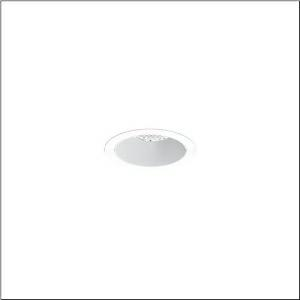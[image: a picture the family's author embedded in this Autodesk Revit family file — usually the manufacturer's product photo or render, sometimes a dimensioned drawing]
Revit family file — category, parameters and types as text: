
# Revit family: lunis_21_m_51db18ec91c
name_source: partatom
category: Lighting Fixtures
units: mm (PartAtom-declared; Revit-internal decimal feet)

## family parameters
Cut with Voids When Loaded = No
Host = Face
Light Source = No
Part Type = Normal
Room Calculation Point = No
Round Connector Dimension = Use Diameter
Shared = No

## types (1)
- --- (1 x LED, 3870 lm, 25.5 W, 6500K)
    Apparent Load = 26 VA
    CIE Flux Codes = 86 95 99 100 100
    Color Rendering = 80
    Color Temperature = 6500K
    Default Elevation = 1800 mm
    Description = Lunis 21 M, downlight, light control with lens, of PMMA, anti glare with reflector, of PC, light emission: direct distribution, LED rated luminous flux: 1.800lm, light colour: 830/840/865, with terminal, 5-pole, mains connection: 220..240V, AC/DC, 0/50..60Hz, housing, round, of diecast aluminium, traffic white (RAL 9016), diameter: 115mm, clamping range: 1..40mm, protection rating (complete): IP20, protection rating (on room side): IP54, insulation class (complete): insulation class II (safety insulation), certification: CE, impact resistance: IK03, packaging unit: 1 piece
    Height = 0 mm  [stored 0 ft]
    Lamp = 1 x LED
    Lamp Light Flux = 3870 lm
    Lamp Power = 25.5 W
    Lamp count = 1
    Length = 115 mm
    Luminous efficacy = 152 lm/W
    Manufacturer = Siteco
    ModVariant = No
    Model = 51DB18EC91C
    Mounting Place = Ceiling
    Mounting Type = Recessed
    Number of Poles = 1
    OnlyDefault = Yes
    Power Factor = 1
    Product Name = Lunis 21 M
    Product group = downlight
    ProductGroupID = 401
    Protection Class = Protection class II
    Protection Degree = IP 20
    RLX_Detail_Level = 1
    RLX_Emergency_Light_Flux = 0 lm
    RLX_Emergency_Type = 0
    RLX_Emergency_Type_DB = No
    RlxData = <blob elided: 14053 chars, md5=98b3849f>
    Socket = socket
    Standby Power = 0 W
    System Light Flux = 3870 lm
    System Power = 26 W
    Type Comments = individual setting: colour temperature 6500K, luminous flux: 100 % | (ON | ON | OFF | OFF) | 700 mA
    Type Image = l_1290852.jpg
    URL = http://relux.com
    VarID = @adj_035393
    Voltage = 0 V
    Weight = 0.00 kg
    Width = 0 mm  [stored 0 ft]

note: [stored X ft] marks values corroborated as IEEE doubles in the binary element streams (Revit-internal decimal feet)

## geometry (parser evidence)
native form markers: Sweep x11
no freeform markers — native parametric forms only
